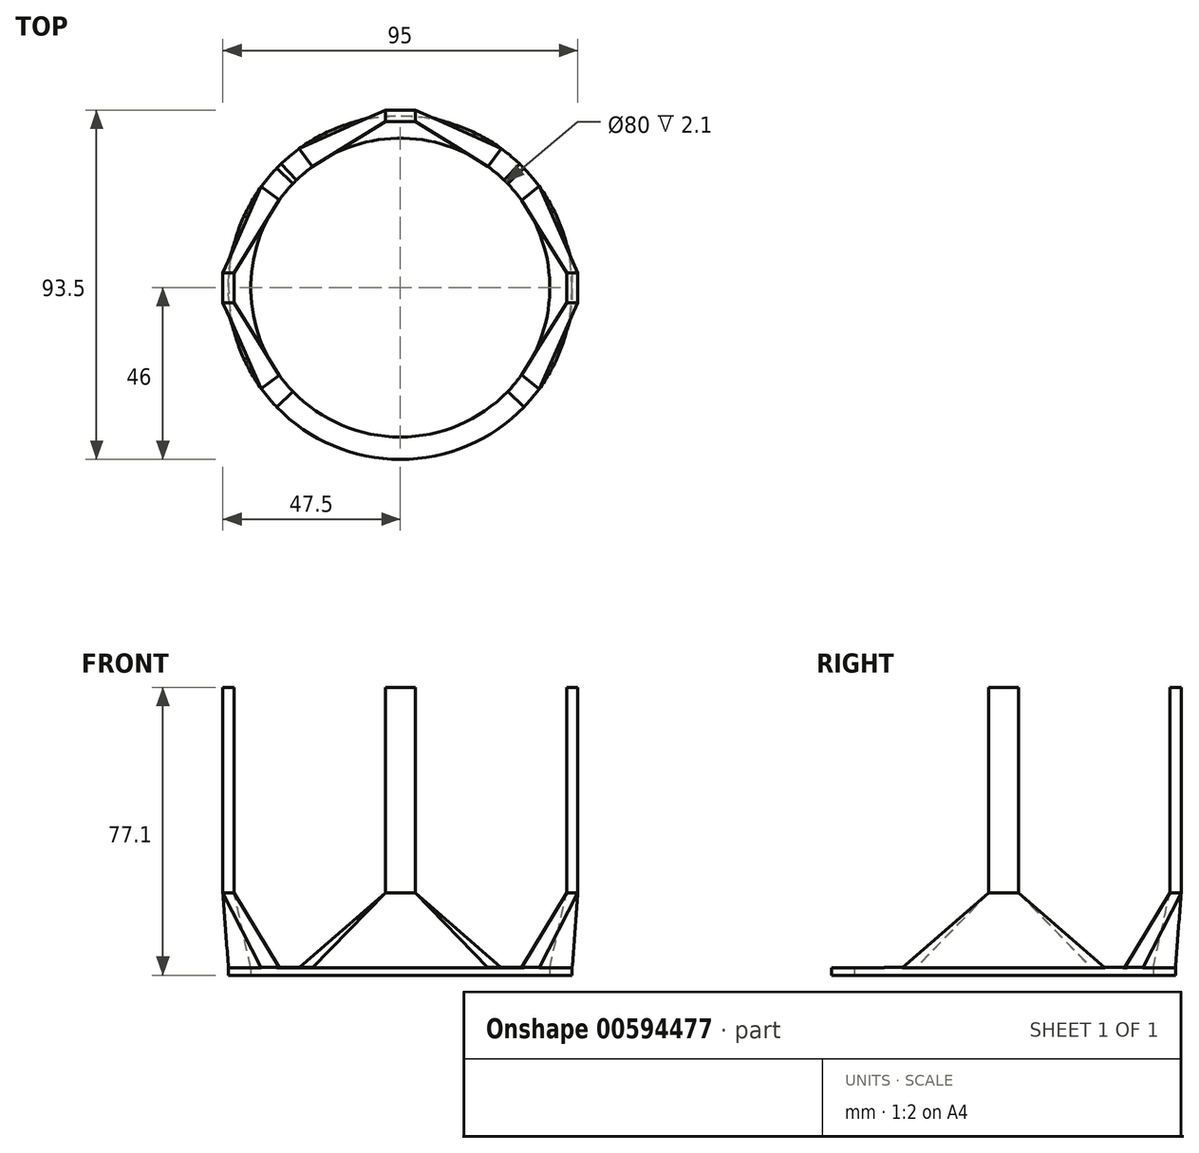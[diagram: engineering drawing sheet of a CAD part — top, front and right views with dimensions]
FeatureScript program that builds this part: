
annotation { "Feature Type Name" : "Feature", "Feature Type Description" : "" }
export const myFeature = defineFeature(function(context is Context, id is Id, definition is map)
    precondition{}
    {
        {
            var Q0;
            Q0=qCreatedBy(makeId("Top.planeOp"),FACE);
            var sketch = newSketch(context, id + "F0", { "sketchPlane" : qUnion([Q0])});
            skCircle(sketch, "E0", {"center": v(0, 0) * mm, "radius": 40 * mm});
            skCircle(sketch, "E1", {"center": v(0, 0) * mm, "radius": 46 * mm});
            skSolve(sketch);
        }
        {
            var Q0;
            Q0=qSketchRegion(id+"F0",true);
            extrude(context, id + "F1", {"entities" : qUnion([Q0]), "depth" : 2 * mm});
        }
        {
            var Q0;
            Q0=makeQuery(id+"F1.opExtrude","CAP_FACE",FACE,{"disambiguationData":[OSD([sQuery(id+"F0.wireOp",EDGE,"E0"),sQuery(id+"F0.wireOp",EDGE,"E1")])],"isStart":false});
            var sketch = newSketch(context, id + "F2", { "sketchPlane" : qUnion([Q0])});
            skLineSegment(sketch, "E2", {"start": v(-42.45, 50.55) * mm, "end": v(44.78, -53.4) * mm, "construction": true});
            skLineSegment(sketch, "E3", {"start": v(-58.3, 48.88) * mm, "end": v(57.86, -48.58) * mm, "construction": true});
            skLineSegment(sketch, "E4", {"start": v(42.45, 50.6) * mm, "end": v(-43.35, -51.65) * mm, "construction": true});
            skLineSegment(sketch, "E5", {"start": v(-32.36, -23.51) * mm, "end": v(-37.22, -27.04) * mm});
            skLineSegment(sketch, "E6", {"start": v(-33.09, -31.95) * mm, "end": v(-28.77, -27.79) * mm});
            skPoint(sketch, "E7.endSnap0", {"position": v(-30.93, -29.87) * mm});
            skLineSegment(sketch, "E8", {"start": v(-46, 0) * mm, "end": v(-40, 0) * mm, "construction": true});
            skLineSegment(sketch, "E9", {"start": v(-33.09, 31.95) * mm, "end": v(-28.77, 27.79) * mm});
            skLineSegment(sketch, "E10", {"start": v(-37.22, 27.04) * mm, "end": v(-32.36, 23.51) * mm});
            skLineSegment(sketch, "E11", {"start": v(-30.93, 29.87) * mm, "end": v(-34.79, 25.27) * mm, "construction": true});
            skLineSegment(sketch, "E12", {"start": v(-27.04, 37.22) * mm, "end": v(-23.51, 32.36) * mm});
            skLineSegment(sketch, "E13", {"start": v(-31.95, 33.09) * mm, "end": v(-27.79, 28.77) * mm});
            skLineSegment(sketch, "E14", {"start": v(-29.87, 30.93) * mm, "end": v(-25.27, 34.79) * mm, "construction": true});
            skLineSegment(sketch, "E15", {"start": v(27.04, 37.22) * mm, "end": v(23.51, 32.36) * mm});
            skLineSegment(sketch, "E16", {"start": v(31.95, 33.1) * mm, "end": v(27.79, 28.77) * mm});
            skLineSegment(sketch, "E17", {"start": v(25.27, 34.79) * mm, "end": v(29.87, 30.93) * mm, "construction": true});
            skLineSegment(sketch, "E18", {"start": v(33.09, 31.96) * mm, "end": v(28.77, 27.79) * mm});
            skLineSegment(sketch, "E19", {"start": v(37.13, 27.15) * mm, "end": v(32.44, 23.4) * mm});
            skLineSegment(sketch, "E20", {"start": v(30.93, 29.87) * mm, "end": v(34.79, 25.28) * mm, "construction": true});
            skLineSegment(sketch, "E21", {"start": v(32.44, -23.4) * mm, "end": v(37.13, -27.15) * mm});
            skLineSegment(sketch, "E22", {"start": v(28.77, -27.79) * mm, "end": v(33.09, -31.96) * mm});
            skLineSegment(sketch, "E23", {"start": v(34.79, -25.28) * mm, "end": v(30.93, -29.87) * mm, "construction": true});
            skLineSegment(sketch, "E24", {"start": v(-30.93, -29.87) * mm, "end": v(-34.79, -25.27) * mm, "construction": true});
            skLineSegment(sketch, "E25", {"start": v(46.13, 38.7) * mm, "end": v(-50.49, -42.37) * mm, "construction": true});
            skArc(sketch, "E26.0", {"start": v(-32.36, -23.51) * mm, "mid": v(-29.26, -27.28) * mm, "end": v(-25.71, -30.64) * mm});
            skArc(sketch, "E27.0", {"start": v(-37.22, -27.04) * mm, "mid": v(-33.64, -31.37) * mm, "end": v(-29.57, -35.24) * mm});
            skArc(sketch, "E28.trimOffspring", {"start": v(-33.09, 31.95) * mm, "mid": v(-35.24, 29.57) * mm, "end": v(-37.22, 27.04) * mm});
            skArc(sketch, "E29.trimOffspring", {"start": v(-28.77, 27.79) * mm, "mid": v(-30.64, 25.71) * mm, "end": v(-32.36, 23.51) * mm});
            skArc(sketch, "E30.trimOffspring", {"start": v(-23.51, 32.36) * mm, "mid": v(-25.71, 30.64) * mm, "end": v(-27.79, 28.77) * mm});
            skArc(sketch, "E31.trimOffspring", {"start": v(-27.04, 37.22) * mm, "mid": v(-29.57, 35.24) * mm, "end": v(-31.95, 33.09) * mm});
            skArc(sketch, "E32.trimOffspring", {"start": v(31.95, 33.1) * mm, "mid": v(29.57, 35.24) * mm, "end": v(27.04, 37.22) * mm});
            skArc(sketch, "E33.trimOffspring", {"start": v(27.79, 28.77) * mm, "mid": v(25.71, 30.64) * mm, "end": v(23.51, 32.36) * mm});
            skArc(sketch, "E34.trimOffspring", {"start": v(32.44, 23.4) * mm, "mid": v(30.69, 25.66) * mm, "end": v(28.77, 27.79) * mm});
            skArc(sketch, "E35.trimOffspring", {"start": v(37.13, 27.15) * mm, "mid": v(35.2, 29.62) * mm, "end": v(33.09, 31.96) * mm});
            skArc(sketch, "E36.trimOffspring", {"start": v(28.77, -27.79) * mm, "mid": v(30.69, -25.66) * mm, "end": v(32.44, -23.4) * mm});
            skArc(sketch, "E37.trimOffspring", {"start": v(33.09, -31.96) * mm, "mid": v(35.2, -29.63) * mm, "end": v(37.13, -27.15) * mm});
            skSolve(sketch);
        }
        {
            var Q0;
            Q0=qSketchRegion(id+"F2",true);
            extrude(context, id + "F3", {"entities" : qUnion([Q0]), "operationType" : NewBodyOperationType.ADD, "depth" : .1 * mm});
        }
        {
            var Q0;
            Q0=makeQuery(id+"F3.opExtrude","CAP_FACE",FACE,{"disambiguationData":[OSD([sQuery(id+"F2.wireOp",EDGE,"99Xpa1VF-T4qT-ukos-qWRp-hoiuqW937heV"),sQuery(id+"F2.wireOp",EDGE,"2uZg2jFw-66yj-KkDT-MyZi-Me08rNZH4T3G"),sQuery(id+"F2.wireOp",EDGE,"E5"),sQuery(id+"F2.wireOp",EDGE,"E6")])],"isStart":false});
            cPlane(context, id + "F4", {"entities" : qUnion([Q0]), "cplaneType" : CPlaneType.OFFSET, "offset" : 20 * mm, "width" : 150 * mm, "height" : 150 * mm});
        }
        {
            var Q0;
            Q0=qCreatedBy(id+"F4.planeOp",FACE);
            var sketch = newSketch(context, id + "F5", { "sketchPlane" : qUnion([Q0])});
            skLineSegment(sketch, "E38.bottom", {"start": v(-44.5, -4) * mm, "end": v(-47.5, -4) * mm});
            skLineSegment(sketch, "E38.top", {"start": v(-44.5, 4) * mm, "end": v(-47.5, 4) * mm});
            skLineSegment(sketch, "E38.left", {"start": v(-44.5, -4) * mm, "end": v(-44.5, 4) * mm});
            skLineSegment(sketch, "E38.right", {"start": v(-47.5, -4) * mm, "end": v(-47.5, 4) * mm});
            skPoint(sketch, "E38.middle", {"position": v(-46, 0) * mm});
            skCircle(sketch, "E39.0", {"center": v(0, 0) * mm, "radius": 49 * mm, "construction": true});
            skCircle(sketch, "E39.1", {"center": v(0, 0) * mm, "radius": 43 * mm, "construction": true});
            skLineSegment(sketch, "E40", {"start": v(-49, 0) * mm, "end": v(-43, 0) * mm, "construction": true});
            skLineSegment(sketch, "E41.bottom", {"start": v(4, 44.5) * mm, "end": v(-4, 44.5) * mm});
            skLineSegment(sketch, "E41.top", {"start": v(4, 47.5) * mm, "end": v(-4, 47.5) * mm});
            skLineSegment(sketch, "E41.left", {"start": v(4, 44.5) * mm, "end": v(4, 47.5) * mm});
            skLineSegment(sketch, "E41.right", {"start": v(-4, 44.5) * mm, "end": v(-4, 47.5) * mm});
            skPoint(sketch, "E41.middle", {"position": v(0, 46) * mm});
            skLineSegment(sketch, "E42", {"start": v(0, 49) * mm, "end": v(0, 43) * mm, "construction": true});
            skLineSegment(sketch, "E43", {"start": v(43, 0) * mm, "end": v(49, 0) * mm, "construction": true});
            skPoint(sketch, "E44", {"position": v(46, 0) * mm});
            skLineSegment(sketch, "E45.bottom", {"start": v(47.5, -4) * mm, "end": v(44.5, -4) * mm});
            skLineSegment(sketch, "E45.top", {"start": v(47.5, 4) * mm, "end": v(44.5, 4) * mm});
            skLineSegment(sketch, "E45.left", {"start": v(47.5, -4) * mm, "end": v(47.5, 4) * mm});
            skLineSegment(sketch, "E45.right", {"start": v(44.5, -4) * mm, "end": v(44.5, 4) * mm});
            skCircle(sketch, "E46", {"center": v(0, 0) * mm, "radius": 46 * mm, "construction": true});
            skSolve(sketch);
        }
        {
            var Q0;
            Q0=qSketchRegion(id+"F5",true);
            extrude(context, id + "F6", {"entities" : qUnion([Q0]), "depth" : 10 * mm});
        }
        {
            var Q0;
            Q0=makeQuery(id+"F6.opExtrude","CAP_FACE",FACE,{"disambiguationData":[OSD([sQuery(id+"F5.wireOp",EDGE,"E38.bottom"),sQuery(id+"F5.wireOp",EDGE,"E38.top"),sQuery(id+"F5.wireOp",EDGE,"E38.left"),sQuery(id+"F5.wireOp",EDGE,"E38.right")])],"isStart":false});
            cPlane(context, id + "F7", {"entities" : qUnion([Q0]), "cplaneType" : CPlaneType.OFFSET, "offset" : 45 * mm, "width" : 150 * mm, "height" : 150 * mm});
        }
        {
            var Q0;
            Q0=qCreatedBy(id+"F7.planeOp",FACE);
            var sketch = newSketch(context, id + "F8", { "sketchPlane" : qUnion([Q0])});
            skLineSegment(sketch, "E47.0.0", {"start": v(-47.5, -4) * mm, "end": v(-44.5, -4) * mm});
            skLineSegment(sketch, "E47.0.1", {"start": v(-44.5, -4) * mm, "end": v(-44.5, 4) * mm});
            skLineSegment(sketch, "E47.0.2", {"start": v(-44.5, 4) * mm, "end": v(-47.5, 4) * mm});
            skLineSegment(sketch, "E47.0.3", {"start": v(-47.5, 4) * mm, "end": v(-47.5, -4) * mm});
            skLineSegment(sketch, "E48.0.0", {"start": v(44.5, -4) * mm, "end": v(47.5, -4) * mm});
            skLineSegment(sketch, "E48.0.1", {"start": v(47.5, -4) * mm, "end": v(47.5, 4) * mm});
            skLineSegment(sketch, "E48.0.2", {"start": v(47.5, 4) * mm, "end": v(44.5, 4) * mm});
            skLineSegment(sketch, "E48.0.3", {"start": v(44.5, 4) * mm, "end": v(44.5, -4) * mm});
            skLineSegment(sketch, "E49.0.0", {"start": v(-4, 44.5) * mm, "end": v(4, 44.5) * mm});
            skLineSegment(sketch, "E49.0.1", {"start": v(4, 44.5) * mm, "end": v(4, 47.5) * mm});
            skLineSegment(sketch, "E49.0.2", {"start": v(4, 47.5) * mm, "end": v(-4, 47.5) * mm});
            skLineSegment(sketch, "E49.0.3", {"start": v(-4, 47.5) * mm, "end": v(-4, 44.5) * mm});
            skSolve(sketch);
        }
        {
            var Q1;
            Q1=makeQuery(id+"F6.opExtrude","CAP_FACE",FACE,{"disambiguationData":[OSD([sQuery(id+"F5.wireOp",EDGE,"E38.bottom"),sQuery(id+"F5.wireOp",EDGE,"E38.top"),sQuery(id+"F5.wireOp",EDGE,"E38.left"),sQuery(id+"F5.wireOp",EDGE,"E38.right")])],"isStart":true});
            var Q2;
            {var subQ0=sQuery(id+"F0.wireOp",EDGE,"E0");var subQ1=sQuery(id+"F0.wireOp",EDGE,"E1");Q2=makeQuery(id+"F3.boolean.opBoolean","SPLIT",FACE,{"disambiguationData":[TD([makeQuery(id+"F3.opExtrude","SWEPT_FACE",FACE,{"disambiguationData":[OSD([sQuery(id+"F2.wireOp",EDGE,"E5")])]})])],"derivedFrom":makeQuery(id+"F1.opExtrude","CAP_FACE",FACE,{"disambiguationData":[OSD([subQ0,subQ1])],"isStart":false})});}
            loft(context, id + "F9", {"operationType" : NewBodyOperationType.ADD, "sheetProfilesArray" : [{ "sheetProfileEntities" : qUnion([Q1]) }, { "sheetProfileEntities" : qUnion([Q2]) }]});
        }
        {
            var Q1;
            Q1=makeQuery(id+"F6.opExtrude","CAP_FACE",FACE,{"disambiguationData":[OSD([sQuery(id+"F5.wireOp",EDGE,"E41.bottom"),sQuery(id+"F5.wireOp",EDGE,"E41.top"),sQuery(id+"F5.wireOp",EDGE,"E41.left"),sQuery(id+"F5.wireOp",EDGE,"E41.right")])],"isStart":true});
            var Q2;
            {var subQ0=sQuery(id+"F0.wireOp",EDGE,"E0");var subQ1=sQuery(id+"F0.wireOp",EDGE,"E1");Q2=makeQuery(id+"F3.boolean.opBoolean","SPLIT",FACE,{"disambiguationData":[TD([makeQuery(id+"F3.opExtrude","SWEPT_FACE",FACE,{"disambiguationData":[OSD([sQuery(id+"F2.wireOp",EDGE,"E12")])]})])],"derivedFrom":makeQuery(id+"F1.opExtrude","CAP_FACE",FACE,{"disambiguationData":[OSD([subQ0,subQ1])],"isStart":false})});}
            loft(context, id + "F10", {"operationType" : NewBodyOperationType.ADD, "sheetProfilesArray" : [{ "sheetProfileEntities" : qUnion([Q1]) }, { "sheetProfileEntities" : qUnion([Q2]) }]});
        }
        {
            var Q1;
            Q1=makeQuery(id+"F6.opExtrude","CAP_FACE",FACE,{"disambiguationData":[OSD([sQuery(id+"F5.wireOp",EDGE,"E45.bottom"),sQuery(id+"F5.wireOp",EDGE,"E45.top"),sQuery(id+"F5.wireOp",EDGE,"E45.left"),sQuery(id+"F5.wireOp",EDGE,"E45.right")])],"isStart":true});
            var Q2;
            {var subQ0=sQuery(id+"F0.wireOp",EDGE,"E1");var subQ1=sQuery(id+"F0.wireOp",EDGE,"E0");Q2=makeQuery(id+"F3.boolean.opBoolean","SPLIT",FACE,{"disambiguationData":[TD([makeQuery(id+"F3.opExtrude","SWEPT_FACE",FACE,{"disambiguationData":[OSD([sQuery(id+"F2.wireOp",EDGE,"E19")])]})])],"derivedFrom":makeQuery(id+"F1.opExtrude","CAP_FACE",FACE,{"disambiguationData":[OSD([subQ1,subQ0])],"isStart":false})});}
            loft(context, id + "F11", {"operationType" : NewBodyOperationType.ADD, "sheetProfilesArray" : [{ "sheetProfileEntities" : qUnion([Q1]) }, { "sheetProfileEntities" : qUnion([Q2]) }]});
        }
        {
            var Q0;
            Q0=qSketchRegion(id+"F8",true);
            var Q1;
            Q1=makeQuery(id+"F6.opExtrude","CAP_FACE",FACE,{"disambiguationData":[OSD([sQuery(id+"F5.wireOp",EDGE,"E41.bottom"),sQuery(id+"F5.wireOp",EDGE,"E41.top"),sQuery(id+"F5.wireOp",EDGE,"E41.left"),sQuery(id+"F5.wireOp",EDGE,"E41.right")])],"isStart":false});
            extrude(context, id + "F12", {"entities" : qUnion([Q0]), "operationType" : NewBodyOperationType.ADD, "endBound" : BoundingType.UP_TO_SURFACE, "oppositeDirection" : true, "endBoundEntityFace" : qUnion([Q1]), "depth" : 25 * mm});
        }
    });
